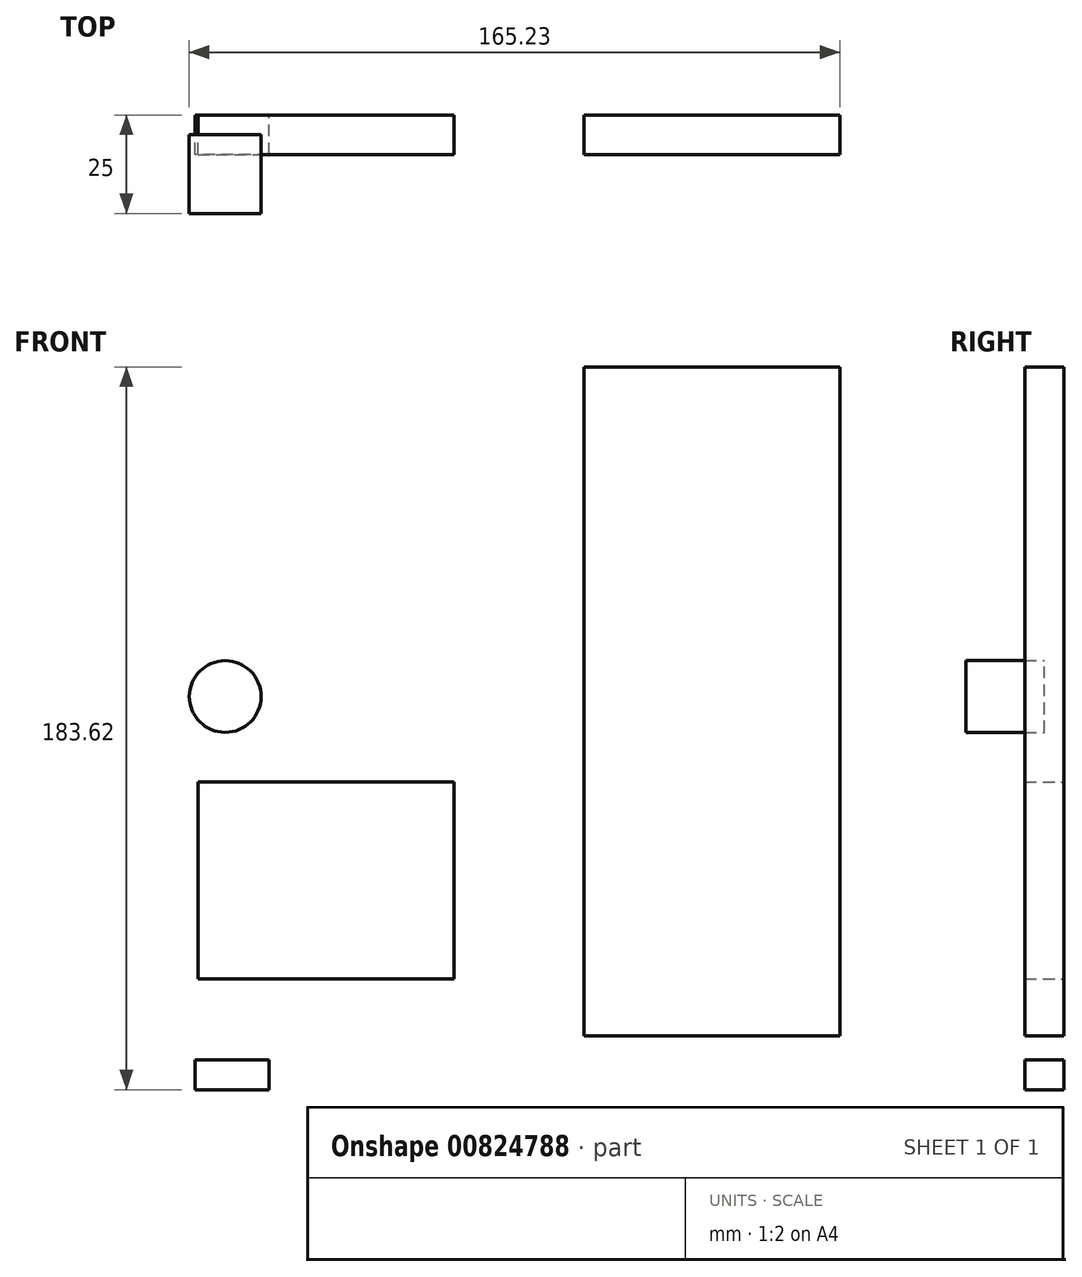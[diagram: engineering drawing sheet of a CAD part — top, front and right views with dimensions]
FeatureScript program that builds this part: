
annotation { "Feature Type Name" : "Feature", "Feature Type Description" : "" }
export const myFeature = defineFeature(function(context is Context, id is Id, definition is map)
    precondition{}
    {
        {
            var Q0;
            Q0=qCreatedBy(makeId("Front.planeOp"),FACE);
            var sketch = newSketch(context, id + "F0", { "sketchPlane" : qUnion([Q0])});
            skLineSegment(sketch, "E0.bottom", {"start": v(-32.5, 25) * mm, "end": v(32.5, 25) * mm});
            skLineSegment(sketch, "E0.top", {"start": v(-32.5, -25) * mm, "end": v(32.5, -25) * mm});
            skLineSegment(sketch, "E0.left", {"start": v(-32.5, 25) * mm, "end": v(-32.5, -25) * mm});
            skLineSegment(sketch, "E0.right", {"start": v(32.5, 25) * mm, "end": v(32.5, -25) * mm});
            skPoint(sketch, "E0.middle", {"position": v(0, 0) * mm});
            skSolve(sketch);
        }
        {
            var Q0;
            Q0 = qSketchRegion(id + "F0", true);
            extrude(context, id + "F1", {"entities" : qUnion([Q0]), "endBound" : BoundingType.SYMMETRIC, "depth" : 10 * mm, "offsetDistance" : 25.4 * mm});
        }
        {
            var Q0;
            Q0=qCreatedBy(makeId("Front.planeOp"),FACE);
            var sketch = newSketch(context, id + "F2", { "sketchPlane" : qUnion([Q0])});
            skLineSegment(sketch, "E1.bottom", {"start": v(65.53, -39.52) * mm, "end": v(130.53, -39.52) * mm});
            skLineSegment(sketch, "E1.top", {"start": v(65.53, 130.48) * mm, "end": v(130.53, 130.48) * mm});
            skLineSegment(sketch, "E1.left", {"start": v(65.53, -39.52) * mm, "end": v(65.53, 130.48) * mm});
            skLineSegment(sketch, "E1.right", {"start": v(130.53, -39.52) * mm, "end": v(130.53, 130.48) * mm});
            skPoint(sketch, "E1.middle", {"position": v(98.03, 45.48) * mm});
            skSolve(sketch);
        }
        {
            var Q0;
            Q0 = qSketchRegion(id + "F2", true);
            var Q1;
            Q1=makeQuery(id+"F2.imprint","IMPRINT",FACE,{"disambiguationData":[TD([[makeQuery(id+"F2.imprint","IMPRINT",EDGE,{"derivedFrom":sQuery(id+"F2.wireOp",EDGE,"E1.bottom")}),1.0]])]});
            extrude(context, id + "F3", {"entities" : qUnion([Q0, Q1]), "endBound" : BoundingType.SYMMETRIC, "depth" : 10 * mm, "offsetDistance" : 25.4 * mm});
        }
        {
            var Q0;
            Q0=qCreatedBy(makeId("Front.planeOp"),FACE);
            var sketch = newSketch(context, id + "F4", { "sketchPlane" : qUnion([Q0])});
            skCircle(sketch, "E2", {"center": v(-25.59, 46.76) * mm, "radius": 9.11 * mm});
            skSolve(sketch);
        }
        {
            var Q0;
            Q0=makeQuery(id+"F4.imprint","IMPRINT",FACE,{"disambiguationData":[TD([[makeQuery(id+"F4.imprint","IMPRINT",EDGE,{"derivedFrom":sQuery(id+"F4.wireOp",EDGE,"E2")}),1.0]])]});
            extrude(context, id + "F5", {"entities" : qUnion([Q0]), "depth" : 20 * mm, "offsetDistance" : 25.4 * mm});
        }
        {
            var Q0;
            Q0=qCreatedBy(makeId("Front.planeOp"),FACE);
            var sketch = newSketch(context, id + "F6", { "sketchPlane" : qUnion([Q0])});
            skLineSegment(sketch, "E3.bottom", {"start": v(-14.42, -53.14) * mm, "end": v(-33.18, -53.14) * mm});
            skLineSegment(sketch, "E3.top", {"start": v(-14.42, -45.55) * mm, "end": v(-33.18, -45.55) * mm});
            skLineSegment(sketch, "E3.left", {"start": v(-14.42, -53.14) * mm, "end": v(-14.42, -45.55) * mm});
            skLineSegment(sketch, "E3.right", {"start": v(-33.18, -53.14) * mm, "end": v(-33.18, -45.55) * mm});
            skPoint(sketch, "E3.middle", {"position": v(-23.8, -49.35) * mm});
            skSolve(sketch);
        }
        {
            var Q0;
            Q0=makeQuery(id+"F6.imprint","IMPRINT",FACE,{"disambiguationData":[TD([[makeQuery(id+"F6.imprint","IMPRINT",EDGE,{"derivedFrom":sQuery(id+"F6.wireOp",EDGE,"E3.bottom")}),-1.0]])]});
            extrude(context, id + "F7", {"entities" : qUnion([Q0]), "endBound" : BoundingType.SYMMETRIC, "depth" : 10 * mm, "offsetDistance" : 25.4 * mm});
        }
    });
